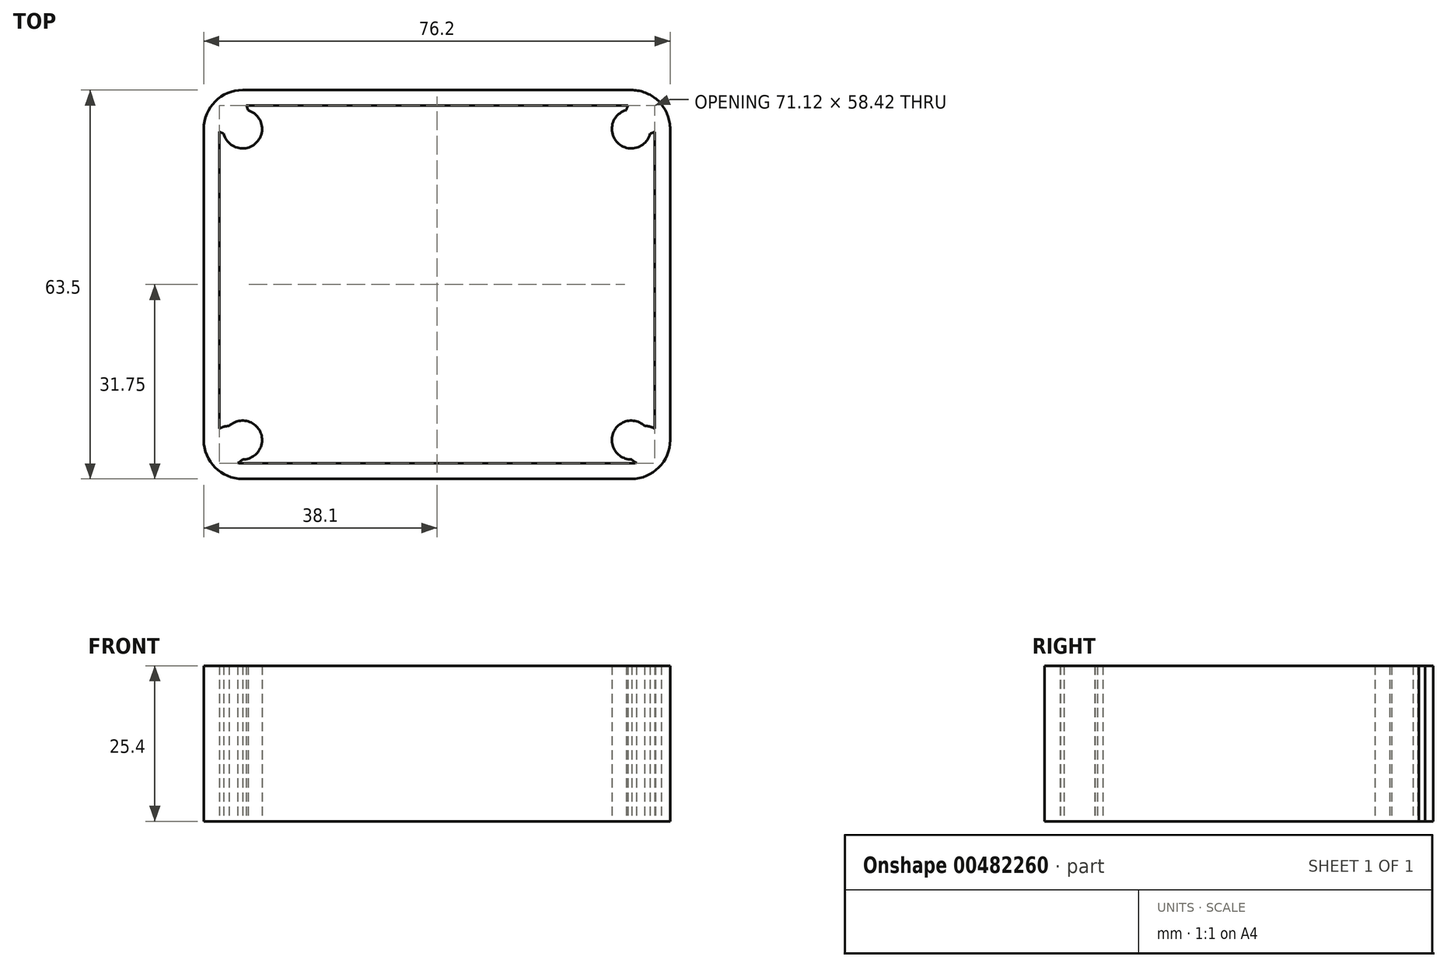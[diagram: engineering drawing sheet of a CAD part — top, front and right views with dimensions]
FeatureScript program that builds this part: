
annotation { "Feature Type Name" : "Feature", "Feature Type Description" : "" }
export const myFeature = defineFeature(function(context is Context, id is Id, definition is map)
    precondition{}
    {
        {
            var Q0;
            Q0=qCreatedBy(makeId("Top.planeOp"),FACE);
            var sketch = newSketch(context, id + "F0", { "sketchPlane" : qUnion([Q0])});
            skLineSegment(sketch, "E0.bottom", {"start": v(31.75, -31.75) * mm, "end": v(-31.75, -31.75) * mm});
            skLineSegment(sketch, "E0.top", {"start": v(31.75, 31.75) * mm, "end": v(-31.75, 31.75) * mm});
            skLineSegment(sketch, "E0.left", {"start": v(38.1, -25.4) * mm, "end": v(38.1, 25.4) * mm});
            skLineSegment(sketch, "E0.right", {"start": v(-38.1, -25.4) * mm, "end": v(-38.1, 25.4) * mm});
            skPoint(sketch, "E0.middle", {"position": v(0, 0) * mm});
            skPoint(sketch, "E1.visualSharp", {"position": v(-38.1, 31.75) * mm});
            skArc(sketch, "E1.filletArc", {"start": v(-31.75, 31.75) * mm, "mid": v(-36.24, 29.9) * mm, "end": v(-38.1, 25.4) * mm});
            skPoint(sketch, "E2.visualSharp", {"position": v(38.1, 31.75) * mm});
            skArc(sketch, "E2.filletArc", {"start": v(38.1, 25.4) * mm, "mid": v(36.24, 29.9) * mm, "end": v(31.75, 31.75) * mm});
            skPoint(sketch, "E3.visualSharp", {"position": v(38.1, -31.75) * mm});
            skArc(sketch, "E3.filletArc", {"start": v(31.75, -31.75) * mm, "mid": v(36.24, -29.9) * mm, "end": v(38.1, -25.4) * mm});
            skPoint(sketch, "E4.visualSharp", {"position": v(-38.1, -31.75) * mm});
            skArc(sketch, "E4.filletArc", {"start": v(-38.1, -25.4) * mm, "mid": v(-36.24, -29.9) * mm, "end": v(-31.75, -31.75) * mm});
            skSolve(sketch);
        }
        {
            var Q0;
            Q0 = qSketchRegion(id + "F0", true);
            extrude(context, id + "F1", {"entities" : qUnion([Q0]), "depth" : 25.4 * mm});
        }
        {
            var Q0;
            Q0=makeQuery(id+"F1.opExtrude","CAP_FACE",FACE,{"disambiguationData":[OSD([sQuery(id+"F0.wireOp",EDGE,"E0.bottom"),sQuery(id+"F0.wireOp",EDGE,"E0.top"),sQuery(id+"F0.wireOp",EDGE,"E0.left"),sQuery(id+"F0.wireOp",EDGE,"E0.right"),sQuery(id+"F0.wireOp",EDGE,"E1.filletArc"),sQuery(id+"F0.wireOp",EDGE,"E2.filletArc"),sQuery(id+"F0.wireOp",EDGE,"E3.filletArc"),sQuery(id+"F0.wireOp",EDGE,"E4.filletArc")])],"isStart":true});
            var Q1;
            Q1=makeQuery(id+"F1.opExtrude","CAP_FACE",FACE,{"disambiguationData":[OSD([sQuery(id+"F0.wireOp",EDGE,"E0.bottom"),sQuery(id+"F0.wireOp",EDGE,"E0.top"),sQuery(id+"F0.wireOp",EDGE,"E0.left"),sQuery(id+"F0.wireOp",EDGE,"E0.right"),sQuery(id+"F0.wireOp",EDGE,"E1.filletArc"),sQuery(id+"F0.wireOp",EDGE,"E2.filletArc"),sQuery(id+"F0.wireOp",EDGE,"E3.filletArc"),sQuery(id+"F0.wireOp",EDGE,"E4.filletArc")])],"isStart":false});
            var Q2;
            Q2=makeQuery(id+"F1.opExtrude","SWEPT_BODY",BODY,{"disambiguationData":[OSD([sQuery(id+"F0.wireOp",EDGE,"E0.bottom"),sQuery(id+"F0.wireOp",EDGE,"E0.top"),sQuery(id+"F0.wireOp",EDGE,"E0.left"),sQuery(id+"F0.wireOp",EDGE,"E0.right"),sQuery(id+"F0.wireOp",EDGE,"E1.filletArc"),sQuery(id+"F0.wireOp",EDGE,"E2.filletArc"),sQuery(id+"F0.wireOp",EDGE,"E3.filletArc"),sQuery(id+"F0.wireOp",EDGE,"E4.filletArc")])]});
            shell(context, id + "F2", {"entities" : qUnion([Q0, Q1]), "parts" : qUnion([Q2]), "thickness" : 2.54 * mm});
        }
        {
            var Q0;
            Q0=qCreatedBy(makeId("Top.planeOp"),FACE);
            var sketch = newSketch(context, id + "F3", { "sketchPlane" : qUnion([Q0])});
            skCircle(sketch, "E5", {"center": v(-31.75, 25.4) * mm, "radius": 3.18 * mm});
            skCircle(sketch, "E6.0.1.0", {"center": v(-31.75, -25.4) * mm, "radius": 3.18 * mm});
            skCircle(sketch, "E6.1.0.0", {"center": v(31.75, 25.4) * mm, "radius": 3.18 * mm});
            skCircle(sketch, "E6.1.1.0", {"center": v(31.75, -25.4) * mm, "radius": 3.18 * mm});
            skLineSegment(sketch, "E6.direction1", {"start": v(-31.75, 25.4) * mm, "end": v(31.75, 25.4) * mm, "construction": true});
            skLineSegment(sketch, "E6.direction2", {"start": v(-31.75, 25.4) * mm, "end": v(-31.75, -25.4) * mm, "construction": true});
            skCircle(sketch, "E7", {"center": v(-33.94, 27.7) * mm, "radius": 3.18 * mm});
            skCircle(sketch, "E8.0.1.0", {"center": v(-33.94, -26.28) * mm, "radius": 3.18 * mm});
            skCircle(sketch, "E8.1.0.0", {"center": v(34, 27.7) * mm, "radius": 3.18 * mm});
            skCircle(sketch, "E8.1.1.0", {"center": v(34, -26.28) * mm, "radius": 3.18 * mm});
            skLineSegment(sketch, "E8.direction1", {"start": v(-33.94, 27.7) * mm, "end": v(34, 27.7) * mm, "construction": true});
            skLineSegment(sketch, "E8.direction2", {"start": v(-33.94, 27.7) * mm, "end": v(-33.94, -26.28) * mm, "construction": true});
            skSolve(sketch);
        }
        {
            var Q0;
            Q0 = qSketchRegion(id + "F3", true);
            extrude(context, id + "F4", {"entities" : qUnion([Q0]), "operationType" : NewBodyOperationType.ADD, "depth" : 25.4 * mm});
        }
    });
